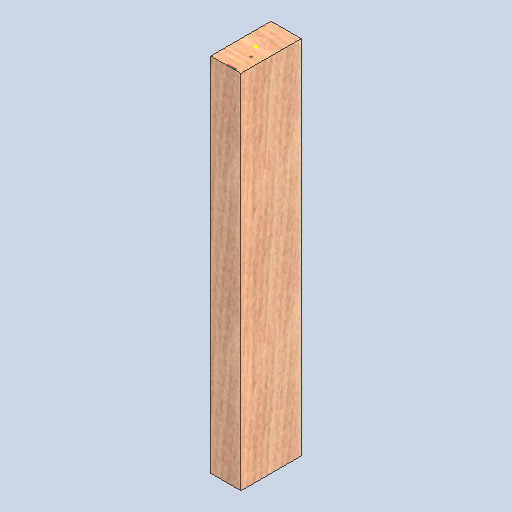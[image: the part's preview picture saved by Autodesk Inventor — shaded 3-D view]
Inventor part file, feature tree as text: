
AUTODESK INVENTOR PART (.ipt)
format: ipt  version: 2025 (Build 290162000, 162)  size: 181,248 bytes
history: native  units: in
note: dims shown in document units (in); Inventor stores cm internally (conversion verified against a paired STEP export)
features: other x3, sketch x2
ambient origin geometry x8: Origin, YZ Plane, XZ Plane, XY Plane, X Axis, Y Axis, Z Axis, Center Point
bodies: Solid1 (feature_tree)
feature tree (5):
  other  "2x4x24.ipt"
  other  "Solid1::2x4x24.ipt"
  other  "TaggingFeature1"
  sketch  "Sketch1"  dims[d0=0.3937in]
  sketch  "Sketch2"
